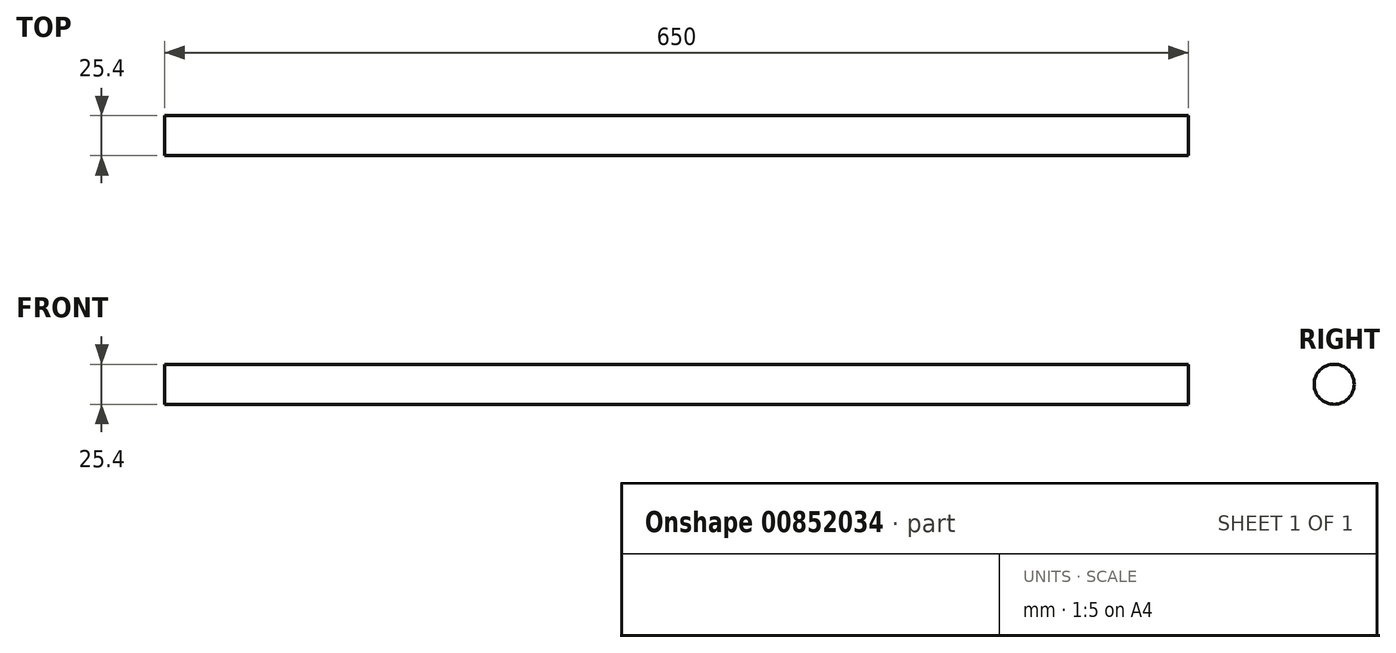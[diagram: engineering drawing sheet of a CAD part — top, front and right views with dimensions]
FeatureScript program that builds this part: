
annotation { "Feature Type Name" : "Feature", "Feature Type Description" : "" }
export const myFeature = defineFeature(function(context is Context, id is Id, definition is map)
    precondition{}
    {
        {
            var Q0;
            Q0=qCreatedBy(makeId("Right.planeOp"),FACE);
            var sketch = newSketch(context, id + "F0", { "sketchPlane" : qUnion([Q0])});
            skCircle(sketch, "E0", {"center": v(0, 0) * mm, "radius": 12.7 * mm});
            skSolve(sketch);
        }
        {
            var Q0;
            Q0=sQuery(id+"F0.wireOp",EDGE,"E0");
            extrude(context, id + "F1", {"bodyType" : ToolBodyType.SURFACE, "surfaceEntities" : qUnion([Q0]), "depth" : 650 * mm, "offsetDistance" : 25.4 * mm});
        }
    });
